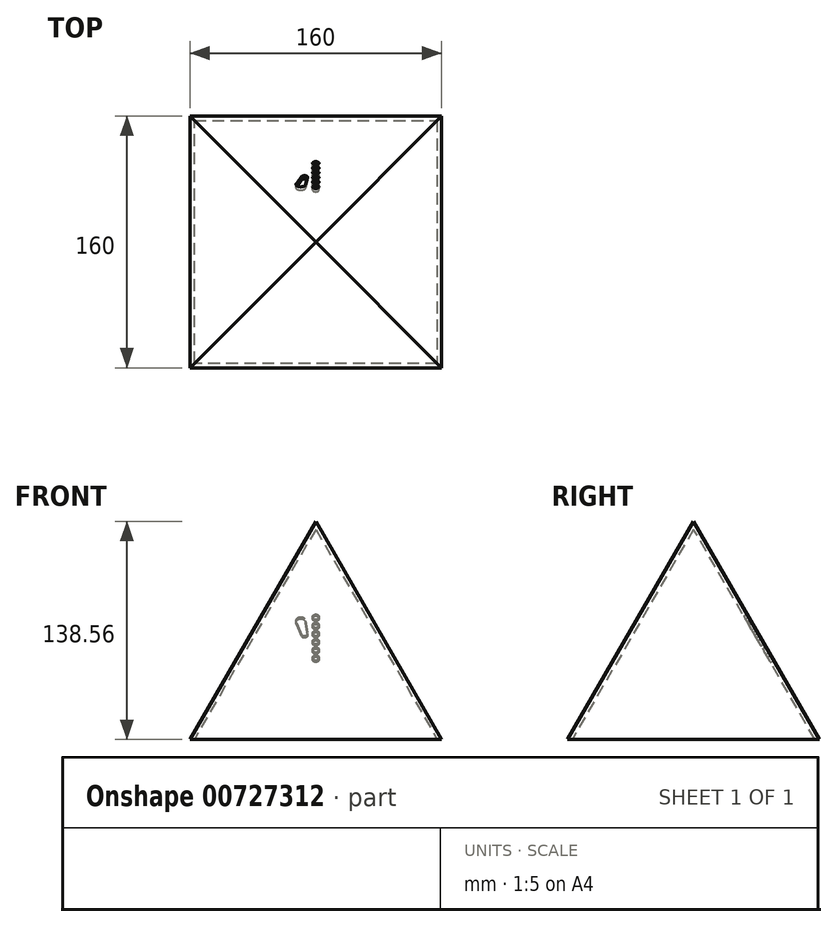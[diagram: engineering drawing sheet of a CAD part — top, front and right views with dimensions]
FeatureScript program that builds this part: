
annotation { "Feature Type Name" : "Feature", "Feature Type Description" : "" }
export const myFeature = defineFeature(function(context is Context, id is Id, definition is map)
    precondition{}
    {
        {
            var Q0;
            Q0=qCreatedBy(makeId("Top.planeOp"),FACE);
            var sketch = newSketch(context, id + "F0", { "sketchPlane" : qUnion([Q0])});
            skLineSegment(sketch, "E0.bottom", {"start": v(-50, 80) * mm, "end": v(50, 80) * mm});
            skLineSegment(sketch, "E0.top", {"start": v(-50, -80) * mm, "end": v(50, -80) * mm});
            skLineSegment(sketch, "E0.left", {"start": v(-80, 50) * mm, "end": v(-80, -50) * mm});
            skLineSegment(sketch, "E0.right", {"start": v(80, 50) * mm, "end": v(80, -50) * mm});
            skPoint(sketch, "E0.middle", {"position": v(0, 0) * mm});
            skLineSegment(sketch, "E1", {"start": v(-50, 80) * mm, "end": v(-50, -80) * mm, "construction": true});
            skLineSegment(sketch, "E2", {"start": v(50, 80) * mm, "end": v(50, -80) * mm, "construction": true});
            skLineSegment(sketch, "E3", {"start": v(80, 50) * mm, "end": v(-80, 50) * mm, "construction": true});
            skLineSegment(sketch, "E4", {"start": v(80, -50) * mm, "end": v(-80, -50) * mm, "construction": true});
            skPoint(sketch, "E5.orphan", {"position": v(-80, 80) * mm});
            skPoint(sketch, "E6.orphan", {"position": v(80, 80) * mm});
            skPoint(sketch, "E7.orphan", {"position": v(80, -80) * mm});
            skPoint(sketch, "E8.orphan", {"position": v(-80, -80) * mm});
            skLineSegment(sketch, "E9", {"start": v(-50, 80) * mm, "end": v(-80, 80) * mm});
            skLineSegment(sketch, "E10", {"start": v(-80, 80) * mm, "end": v(-80, 50) * mm});
            skLineSegment(sketch, "E11", {"start": v(80, 50) * mm, "end": v(80, 80) * mm});
            skLineSegment(sketch, "E12", {"start": v(80, 80) * mm, "end": v(50, 80) * mm});
            skLineSegment(sketch, "E13", {"start": v(80, -50) * mm, "end": v(80, -80) * mm});
            skLineSegment(sketch, "E14", {"start": v(80, -80) * mm, "end": v(50, -80) * mm});
            skLineSegment(sketch, "E15", {"start": v(-50, -80) * mm, "end": v(-80, -80) * mm});
            skLineSegment(sketch, "E16", {"start": v(-80, -80) * mm, "end": v(-80, -50) * mm});
            skSolve(sketch);
        }
        {
            var Q0;
            Q0=makeQuery(id+"F0.imprint","IMPRINT",FACE,{"disambiguationData":[TD([[makeQuery(id+"F0.imprint","IMPRINT",EDGE,{"derivedFrom":sQuery(id+"F0.wireOp",EDGE,"E0.bottom")}),-1.0]])]});
            extrude(context, id + "F1", {"entities" : qUnion([Q0]), "depth" : 139 * mm, "hasDraft" : true, "draftAngle" : 30 * degree, "draftPullDirection" : true});
        }
        {
            var Q0;
            Q0=makeQuery(id+"F1.opExtrude","CAP_FACE",FACE,{"disambiguationData":[OSD([sQuery(id+"F0.wireOp",EDGE,"E0.bottom"),sQuery(id+"F0.wireOp",EDGE,"E0.top"),sQuery(id+"F0.wireOp",EDGE,"E0.left"),sQuery(id+"F0.wireOp",EDGE,"E0.right"),sQuery(id+"F0.wireOp",EDGE,"E9"),sQuery(id+"F0.wireOp",EDGE,"E10"),sQuery(id+"F0.wireOp",EDGE,"E11"),sQuery(id+"F0.wireOp",EDGE,"E12"),sQuery(id+"F0.wireOp",EDGE,"E13"),sQuery(id+"F0.wireOp",EDGE,"E14"),sQuery(id+"F0.wireOp",EDGE,"E15"),sQuery(id+"F0.wireOp",EDGE,"E16")])],"isStart":true});
            shell(context, id + "F2", {"entities" : qUnion([Q0]), "thickness" : 2.5 * mm});
        }
        {
            var Q0;
            Q0=makeQuery(id+"F1.opExtrude","SWEPT_FACE",FACE,{"disambiguationData":[OSD([sQuery(id+"F0.wireOp",EDGE,"E0.bottom"),sQuery(id+"F0.wireOp",EDGE,"E9"),sQuery(id+"F0.wireOp",EDGE,"E12")])]});
            var sketch = newSketch(context, id + "F3", { "sketchPlane" : qUnion([Q0])});
            skCircle(sketch, "E17", {"center": v(0, 20) * mm, "radius": 33 * mm});
            skSolve(sketch);
        }
        {
            var Q0;
            Q0=makeQuery(id+"F3.imprint","IMPRINT",FACE,{"disambiguationData":[TD([[makeQuery(id+"F3.imprint","IMPRINT",EDGE,{"derivedFrom":sQuery(id+"F3.wireOp",EDGE,"E17")}),-1.0]])]});
            var sketch = newSketch(context, id + "F4", { "sketchPlane" : qUnion([Q0])});
            skCircle(sketch, "E18.0", {"center": v(0, 20) * mm, "radius": 33 * mm});
            skCircle(sketch, "E19", {"center": v(0, 26) * mm, "radius": 2 * mm});
            skCircle(sketch, "E20", {"center": v(0, 32) * mm, "radius": 2 * mm});
            skCircle(sketch, "E21", {"center": v(0, 38) * mm, "radius": 2 * mm});
            skCircle(sketch, "E22", {"center": v(0, 44) * mm, "radius": 2 * mm});
            skCircle(sketch, "E23", {"center": v(0, 50) * mm, "radius": 2 * mm});
            skArc(sketch, "E24", {"start": v(11.88, 45.12) * mm, "mid": v(10.51, 49.82) * mm, "end": v(6.53, 46.99) * mm});
            skLineSegment(sketch, "E25", {"start": v(6.53, 46.99) * mm, "end": v(5.2, 37.98) * mm});
            skArc(sketch, "E26", {"start": v(5.25, 38.3) * mm, "mid": v(6.64, 35.92) * mm, "end": v(9.09, 37.18) * mm});
            skLineSegment(sketch, "E27", {"start": v(11.88, 45.12) * mm, "end": v(9.09, 37.18) * mm});
            skSolve(sketch);
        }
        {
            var Q0;
            Q0=makeQuery(id+"F4.imprint","IMPRINT",FACE,{"disambiguationData":[TD([[makeQuery(id+"F4.imprint","IMPRINT",EDGE,{"derivedFrom":sQuery(id+"F4.wireOp",EDGE,"E23")}),1.0]])]});
            var Q1;
            Q1=makeQuery(id+"F4.imprint","IMPRINT",FACE,{"disambiguationData":[TD([[makeQuery(id+"F4.imprint","IMPRINT",EDGE,{"derivedFrom":sQuery(id+"F4.wireOp",EDGE,"E22")}),1.0]])]});
            var Q2;
            Q2=makeQuery(id+"F4.imprint","IMPRINT",FACE,{"disambiguationData":[TD([[makeQuery(id+"F4.imprint","IMPRINT",EDGE,{"derivedFrom":sQuery(id+"F4.wireOp",EDGE,"E21")}),1.0]])]});
            var Q3;
            Q3=makeQuery(id+"F4.imprint","IMPRINT",FACE,{"disambiguationData":[TD([[makeQuery(id+"F4.imprint","IMPRINT",EDGE,{"derivedFrom":sQuery(id+"F4.wireOp",EDGE,"E20")}),1.0]])]});
            var Q4;
            Q4=makeQuery(id+"F4.imprint","IMPRINT",FACE,{"disambiguationData":[TD([[makeQuery(id+"F4.imprint","IMPRINT",EDGE,{"derivedFrom":sQuery(id+"F4.wireOp",EDGE,"E19")}),1.0]])]});
            extrude(context, id + "F5", {"entities" : qUnion([Q0, Q1, Q2, Q3, Q4]), "operationType" : NewBodyOperationType.REMOVE, "endBound" : BoundingType.UP_TO_NEXT, "oppositeDirection" : true, "depth" : 25 * mm});
        }
        {
            var Q0;
            {var subQ5=sQuery(id+"F4.wireOp",EDGE,"E24");Q0=makeQuery(id+"F4.imprint","IMPRINT",FACE,{"disambiguationData":[TD([[makeQuery(id+"F4.imprint","IMPRINT",EDGE,{"derivedFrom":subQ5}),1.0]])]});}
            extrude(context, id + "F6", {"entities" : qUnion([Q0]), "operationType" : NewBodyOperationType.REMOVE, "endBound" : BoundingType.UP_TO_NEXT, "oppositeDirection" : true, "depth" : 25 * mm});
        }
        {
            var Q0;
            Q0=makeQuery(id+"F1.opExtrude","SWEPT_FACE",FACE,{"disambiguationData":[OSD([sQuery(id+"F0.wireOp",EDGE,"E0.bottom"),sQuery(id+"F0.wireOp",EDGE,"E9"),sQuery(id+"F0.wireOp",EDGE,"E12")])]});
            var sketch = newSketch(context, id + "F7", { "sketchPlane" : qUnion([Q0])});
            skCircle(sketch, "E28", {"center": v(0, 20) * mm, "radius": 2 * mm});
            skSolve(sketch);
        }
        {
            var Q0;
            Q0=makeQuery(id+"F7.imprint","IMPRINT",FACE,{"disambiguationData":[TD([[makeQuery(id+"F7.imprint","IMPRINT",EDGE,{"derivedFrom":sQuery(id+"F7.wireOp",EDGE,"E28")}),1.0]])]});
            extrude(context, id + "F8", {"entities" : qUnion([Q0]), "operationType" : NewBodyOperationType.REMOVE, "endBound" : BoundingType.UP_TO_NEXT, "oppositeDirection" : true, "depth" : 25 * mm});
        }
    });
